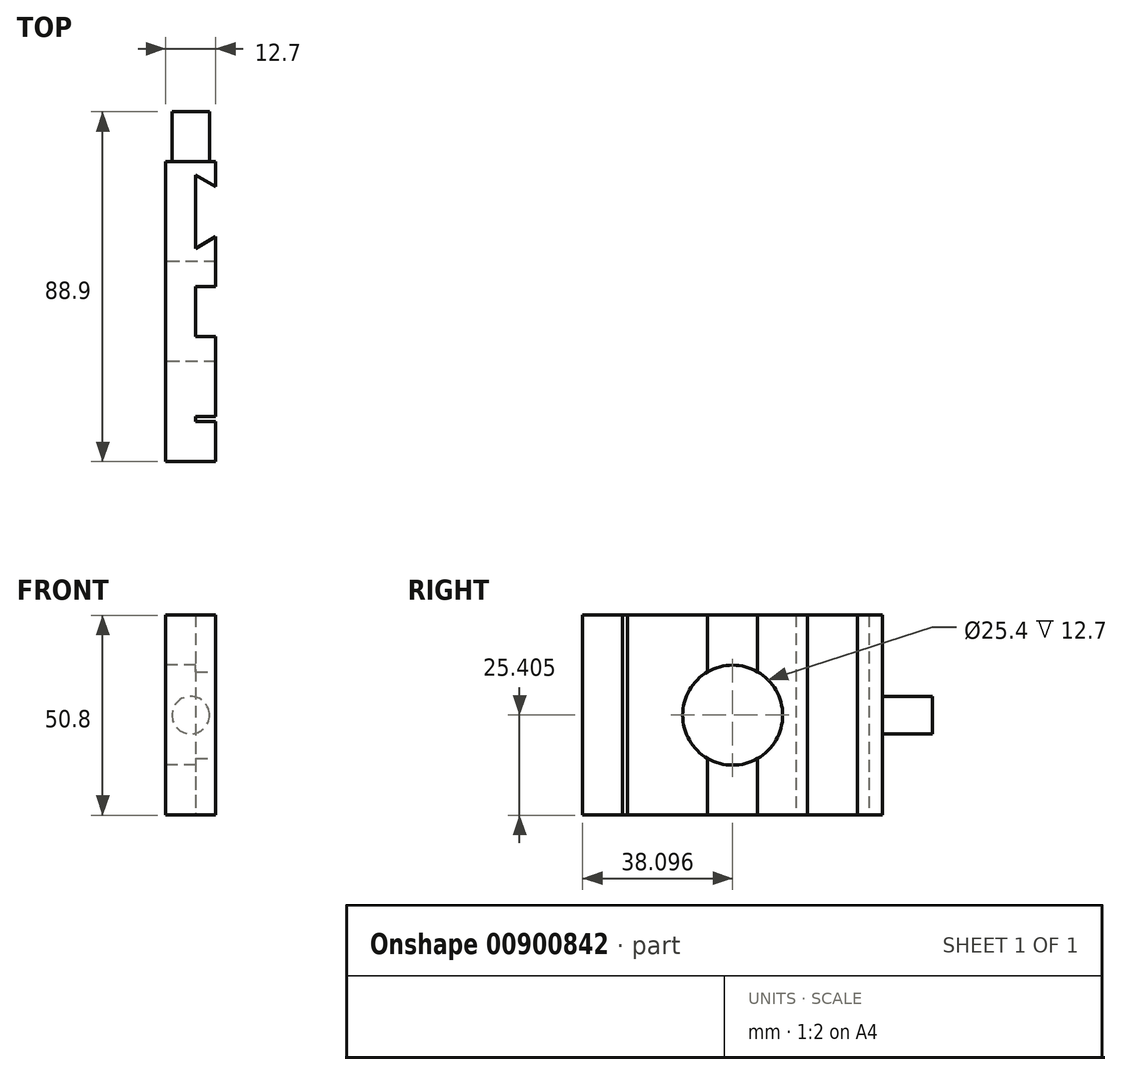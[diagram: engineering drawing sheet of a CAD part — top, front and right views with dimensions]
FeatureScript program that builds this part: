
annotation { "Feature Type Name" : "Feature", "Feature Type Description" : "" }
export const myFeature = defineFeature(function(context is Context, id is Id, definition is map)
    precondition{}
    {
        {
            var Q0;
            Q0=qCreatedBy(makeId("Right.planeOp"),FACE);
            var sketch = newSketch(context, id + "F0", { "sketchPlane" : qUnion([Q0])});
            skCircle(sketch, "E0", {"center": v(36.59, -18.7) * mm, "radius": 12.7 * mm});
            skLineSegment(sketch, "E1.bottom", {"start": v(74.69, -44.1) * mm, "end": v(-1.51, -44.1) * mm});
            skLineSegment(sketch, "E1.top", {"start": v(74.69, 6.7) * mm, "end": v(-1.51, 6.7) * mm});
            skLineSegment(sketch, "E1.left", {"start": v(74.69, -44.1) * mm, "end": v(74.69, 6.7) * mm});
            skLineSegment(sketch, "E1.right", {"start": v(-1.51, -44.1) * mm, "end": v(-1.51, 6.7) * mm});
            skSolve(sketch);
        }
        {
            var Q0;
            Q0=makeQuery(id+"F0.imprint","IMPRINT",FACE,{"disambiguationData":[TD([[makeQuery(id+"F0.imprint","IMPRINT",EDGE,{"derivedFrom":sQuery(id+"F0.wireOp",EDGE,"E0")}),-1.0]])]});
            extrude(context, id + "F1", {"entities" : qUnion([Q0]), "depth" : 12.7 * mm, "offsetDistance" : 25.4 * mm});
        }
        {
            var Q0;
            Q0=makeQuery(id+"F1.opExtrude","CAP_FACE",FACE,{"disambiguationData":[OSD([sQuery(id+"F0.wireOp",EDGE,"E0"),sQuery(id+"F0.wireOp",EDGE,"E1.bottom"),sQuery(id+"F0.wireOp",EDGE,"E1.top"),sQuery(id+"F0.wireOp",EDGE,"E1.left"),sQuery(id+"F0.wireOp",EDGE,"E1.right")])],"isStart":false});
            var sketch = newSketch(context, id + "F2", { "sketchPlane" : qUnion([Q0])});
            skLineSegment(sketch, "E2.bottom", {"start": v(8.65, 6.7) * mm, "end": v(9.92, 6.7) * mm});
            skLineSegment(sketch, "E2.top", {"start": v(8.65, -44.1) * mm, "end": v(9.92, -44.1) * mm});
            skLineSegment(sketch, "E2.left", {"start": v(8.65, 6.7) * mm, "end": v(8.65, -44.1) * mm});
            skLineSegment(sketch, "E2.right", {"start": v(9.92, 6.7) * mm, "end": v(9.92, -44.1) * mm});
            skLineSegment(sketch, "E3", {"start": v(30.24, 6.7) * mm, "end": v(30.24, -44.1) * mm});
            skLineSegment(sketch, "E4", {"start": v(30.24, -44.1) * mm, "end": v(42.94, -44.1) * mm});
            skLineSegment(sketch, "E5", {"start": v(42.94, -44.1) * mm, "end": v(42.94, 6.7) * mm});
            skLineSegment(sketch, "E6", {"start": v(42.94, 6.7) * mm, "end": v(30.24, 6.7) * mm});
            skPoint(sketch, "E7", {"position": v(36.59, -18.7) * mm});
            skLineSegment(sketch, "E8", {"start": v(36.59, 6.7) * mm, "end": v(36.59, -44.1) * mm, "construction": true});
            skSolve(sketch);
        }
        {
            var Q0;
            Q0=makeQuery(id+"F2.imprint","IMPRINT",FACE,{"disambiguationData":[TD([[makeQuery(id+"F2.imprint","IMPRINT",EDGE,{"derivedFrom":sQuery(id+"F2.wireOp",EDGE,"E2.bottom")}),1.0]])]});
            var Q1;
            {var subQ0=sQuery(id+"F2.wireOp",EDGE,"E6");Q1=makeQuery(id+"F2.imprint","IMPRINT",FACE,{"disambiguationData":[TD([[makeQuery(id+"F2.imprint","IMPRINT",EDGE,{"derivedFrom":subQ0}),1.0]])]});}
            var Q2;
            {var subQ0=sQuery(id+"F2.wireOp",EDGE,"E4");Q2=makeQuery(id+"F2.imprint","IMPRINT",FACE,{"disambiguationData":[TD([[makeQuery(id+"F2.imprint","IMPRINT",EDGE,{"derivedFrom":subQ0}),-1.0]])]});}
            extrude(context, id + "F3", {"entities" : qUnion([Q0, Q1, Q2]), "operationType" : NewBodyOperationType.REMOVE, "oppositeDirection" : true, "depth" : 5.08 * mm, "offsetDistance" : 25.4 * mm});
        }
        {
            var Q0;
            Q0=makeQuery(id+"F1.opExtrude","SWEPT_FACE",FACE,{"disambiguationData":[OSD([sQuery(id+"F0.wireOp",EDGE,"E1.bottom")])]});
            var sketch = newSketch(context, id + "F4", { "sketchPlane" : qUnion([Q0])});
            skLineSegment(sketch, "E9", {"start": v(12.7, -55.64) * mm, "end": v(7.62, -52.7) * mm});
            skLineSegment(sketch, "E10", {"start": v(7.62, -52.7) * mm, "end": v(7.62, -71.27) * mm});
            skLineSegment(sketch, "E11", {"start": v(7.62, -71.27) * mm, "end": v(12.7, -68.34) * mm});
            skLineSegment(sketch, "E12", {"start": v(12.7, -68.34) * mm, "end": v(12.7, -55.64) * mm});
            skLineSegment(sketch, "E13", {"start": v(7.62, -61.99) * mm, "end": v(12.7, -61.99) * mm, "construction": true});
            skSolve(sketch);
        }
        {
            var Q0;
            Q0=makeQuery(id+"F4.imprint","IMPRINT",FACE,{"disambiguationData":[TD([[makeQuery(id+"F4.imprint","IMPRINT",EDGE,{"derivedFrom":sQuery(id+"F4.wireOp",EDGE,"E9")}),1.0]])]});
            extrude(context, id + "F5", {"entities" : qUnion([Q0]), "operationType" : NewBodyOperationType.REMOVE, "endBound" : BoundingType.THROUGH_ALL, "oppositeDirection" : true, "depth" : 25.4 * mm, "offsetDistance" : 25.4 * mm});
        }
        {
            var Q0;
            Q0=makeQuery(id+"F1.opExtrude","SWEPT_FACE",FACE,{"disambiguationData":[OSD([sQuery(id+"F0.wireOp",EDGE,"E1.left")])]});
            var sketch = newSketch(context, id + "F6", { "sketchPlane" : qUnion([Q0])});
            skCircle(sketch, "E14", {"center": v(-6.35, -18.7) * mm, "radius": 4.76 * mm});
            skPoint(sketch, "E14.centerSnap0", {"position": v(-6.35, -44.1) * mm});
            skPoint(sketch, "E14.centerSnap1", {"position": v(-12.7, -18.7) * mm});
            skSolve(sketch);
        }
        {
            var Q0;
            Q0=makeQuery(id+"F6.imprint","IMPRINT",FACE,{"disambiguationData":[TD([[makeQuery(id+"F6.imprint","IMPRINT",EDGE,{"derivedFrom":sQuery(id+"F6.wireOp",EDGE,"E14")}),1.0]])]});
            extrude(context, id + "F7", {"entities" : qUnion([Q0]), "operationType" : NewBodyOperationType.ADD, "depth" : 12.7 * mm, "offsetDistance" : 25.4 * mm});
        }
    });
